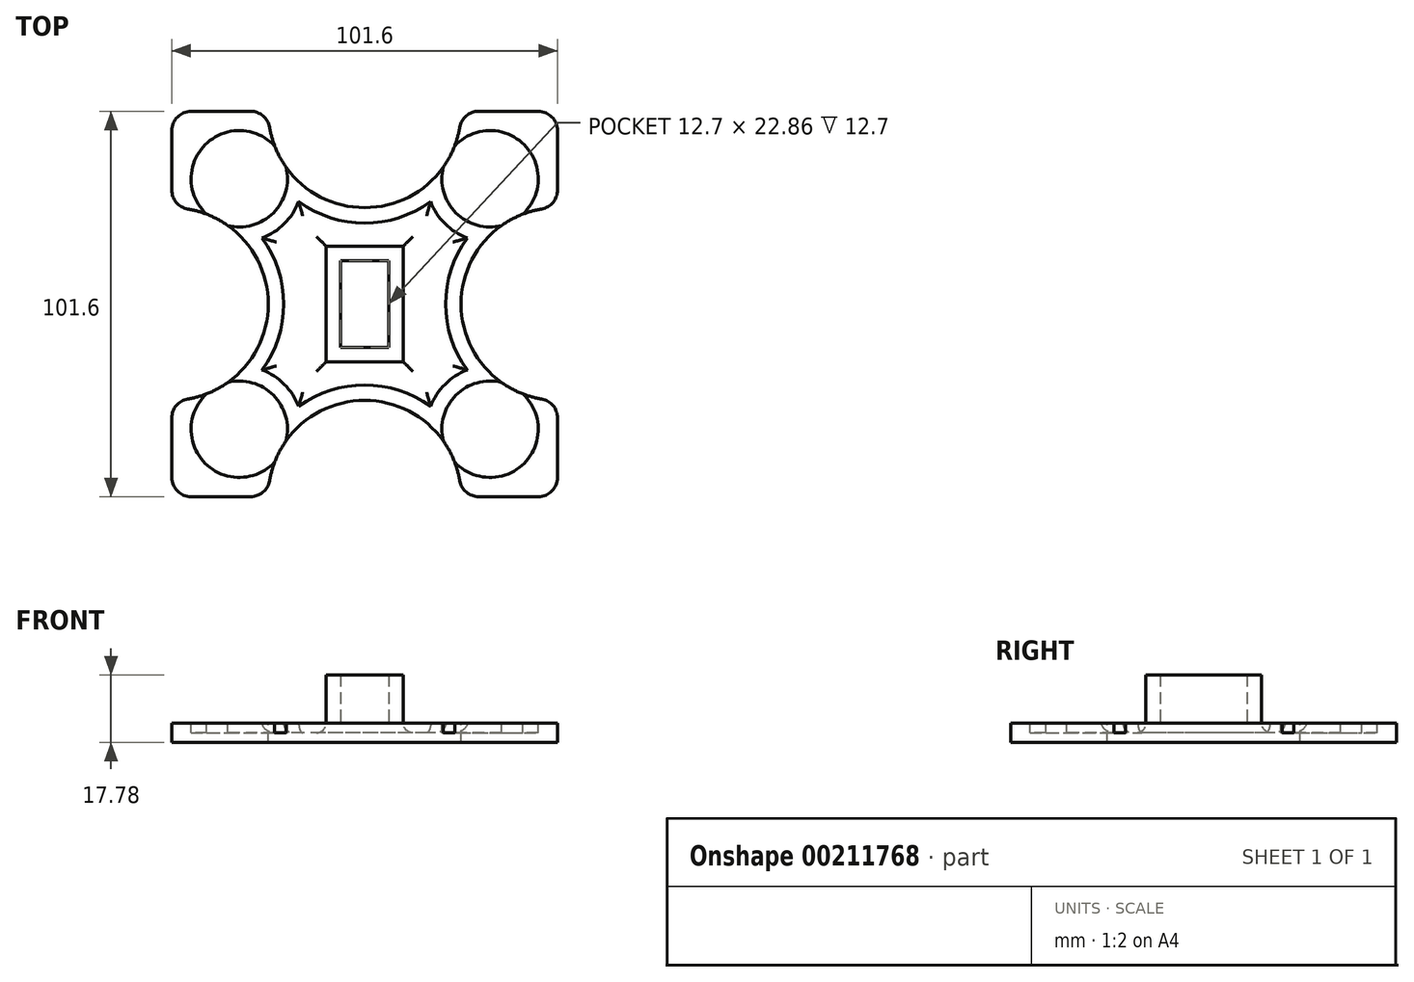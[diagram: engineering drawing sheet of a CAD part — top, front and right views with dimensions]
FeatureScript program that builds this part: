
annotation { "Feature Type Name" : "Feature", "Feature Type Description" : "" }
export const myFeature = defineFeature(function(context is Context, id is Id, definition is map)
    precondition{}
    {
        {
            var Q0;
            Q0=qCreatedBy(makeId("Top.planeOp"),FACE);
            var sketch = newSketch(context, id + "F0", { "sketchPlane" : qUnion([Q0])});
            skLineSegment(sketch, "E0.bottom", {"start": v(50.8, 50.8) * mm, "end": v(-50.8, 50.8) * mm});
            skLineSegment(sketch, "E0.top", {"start": v(50.8, -50.8) * mm, "end": v(-50.8, -50.8) * mm});
            skLineSegment(sketch, "E0.left", {"start": v(50.8, 50.8) * mm, "end": v(50.8, -50.8) * mm});
            skLineSegment(sketch, "E0.right", {"start": v(-50.8, 50.8) * mm, "end": v(-50.8, -50.8) * mm});
            skPoint(sketch, "E0.middle", {"position": v(0, 0) * mm});
            skSolve(sketch);
        }
        {
            var Q0;
            Q0 = qSketchRegion(id + "F0", true);
            var Q1;
            Q1=makeQuery(id+"F0.imprint","IMPRINT",FACE,{"disambiguationData":[TD([[makeQuery(id+"F0.imprint","IMPRINT",EDGE,{"derivedFrom":sQuery(id+"F0.wireOp",EDGE,"E0.bottom")}),1.0]])]});
            extrude(context, id + "F1", {"entities" : qUnion([Q0, Q1]), "depth" : 5.08 * mm});
        }
        {
            var Q0;
            Q0=makeQuery(id+"F1.opExtrude","CAP_FACE",FACE,{"disambiguationData":[OSD([sQuery(id+"F0.wireOp",EDGE,"E0.bottom"),sQuery(id+"F0.wireOp",EDGE,"E0.top"),sQuery(id+"F0.wireOp",EDGE,"E0.left"),sQuery(id+"F0.wireOp",EDGE,"E0.right")])],"isStart":false});
            var sketch = newSketch(context, id + "F2", { "sketchPlane" : qUnion([Q0])});
            skCircle(sketch, "E1", {"center": v(-33.02, 33.02) * mm, "radius": 12.7 * mm});
            skLineSegment(sketch, "E2", {"start": v(0, 54.58) * mm, "end": v(0, -59.94) * mm, "construction": true});
            skLineSegment(sketch, "E3", {"start": v(0, -59.94) * mm, "end": v(60.03, 0) * mm, "construction": true});
            skLineSegment(sketch, "E4", {"start": v(60.03, 0) * mm, "end": v(-63.32, 0) * mm, "construction": true});
            skPoint(sketch, "E4.endSnap0", {"position": v(-50.8, 0) * mm});
            skCircle(sketch, "E5.MirrorC", {"center": v(33.02, 33.02) * mm, "radius": 12.7 * mm});
            skCircle(sketch, "E6.MirrorC", {"center": v(33.02, -33.02) * mm, "radius": 12.7 * mm});
            skCircle(sketch, "E7.MirrorC", {"center": v(-33.02, -33.02) * mm, "radius": 12.7 * mm});
            skSolve(sketch);
        }
        {
            var Q0;
            Q0 = qSketchRegion(id + "F2", true);
            extrude(context, id + "F3", {"entities" : qUnion([Q0]), "operationType" : NewBodyOperationType.REMOVE, "oppositeDirection" : true, "depth" : 2.54 * mm});
        }
        {
            var Q0;
            Q0=makeQuery(id+"F1.opExtrude","CAP_FACE",FACE,{"disambiguationData":[OSD([sQuery(id+"F0.wireOp",EDGE,"E0.bottom"),sQuery(id+"F0.wireOp",EDGE,"E0.top"),sQuery(id+"F0.wireOp",EDGE,"E0.left"),sQuery(id+"F0.wireOp",EDGE,"E0.right")])],"isStart":false});
            var sketch = newSketch(context, id + "F4", { "sketchPlane" : qUnion([Q0])});
            skLineSegment(sketch, "E8.bottom", {"start": v(6.35, 11.43) * mm, "end": v(-6.35, 11.43) * mm});
            skLineSegment(sketch, "E8.top", {"start": v(6.35, -11.43) * mm, "end": v(-6.35, -11.43) * mm});
            skLineSegment(sketch, "E8.left", {"start": v(6.35, 11.43) * mm, "end": v(6.35, -11.43) * mm});
            skLineSegment(sketch, "E8.right", {"start": v(-6.35, 11.43) * mm, "end": v(-6.35, -11.43) * mm});
            skPoint(sketch, "E8.middle", {"position": v(0, 0) * mm});
            skLineSegment(sketch, "E9.0", {"start": v(10.16, 15.24) * mm, "end": v(-10.16, 15.24) * mm});
            skLineSegment(sketch, "E9.1", {"start": v(10.16, 15.24) * mm, "end": v(10.16, -15.24) * mm});
            skLineSegment(sketch, "E9.2", {"start": v(10.16, -15.24) * mm, "end": v(-10.16, -15.24) * mm});
            skLineSegment(sketch, "E9.3", {"start": v(-10.16, 15.24) * mm, "end": v(-10.16, -15.24) * mm});
            skSolve(sketch);
        }
        {
            var Q0;
            Q0 = qSketchRegion(id + "F4", true);
            extrude(context, id + "F5", {"entities" : qUnion([Q0]), "operationType" : NewBodyOperationType.ADD, "depth" : 12.7 * mm});
        }
        {
            var Q0;
            {var subQ0=sQuery(id+"F0.wireOp",EDGE,"E0.top");var subQ1=sQuery(id+"F0.wireOp",EDGE,"E0.bottom");var subQ2=sQuery(id+"F0.wireOp",EDGE,"E0.left");var subQ3=sQuery(id+"F0.wireOp",EDGE,"E0.right");Q0=makeQuery(id+"F5.boolean.opBoolean","SPLIT",FACE,{"disambiguationData":[TD([makeQuery(id+"F1.opExtrude","SWEPT_FACE",FACE,{"disambiguationData":[OSD([subQ1])]})])],"derivedFrom":makeQuery(id+"F1.opExtrude","CAP_FACE",FACE,{"disambiguationData":[OSD([subQ1,subQ0,subQ2,subQ3])],"isStart":false})});}
            var sketch = newSketch(context, id + "F6", { "sketchPlane" : qUnion([Q0])});
            skCircle(sketch, "E10", {"center": v(-50.8, 0) * mm, "radius": 25.4 * mm});
            skCircle(sketch, "E11.MirrorC", {"center": v(50.8, 0) * mm, "radius": 25.4 * mm});
            skCircle(sketch, "E12", {"center": v(0, 50.8) * mm, "radius": 25.4 * mm});
            skCircle(sketch, "E13", {"center": v(0, -50.8) * mm, "radius": 25.4 * mm});
            skSolve(sketch);
        }
        {
            var Q0;
            Q0 = qSketchRegion(id + "F6", true);
            extrude(context, id + "F7", {"entities" : qUnion([Q0]), "operationType" : NewBodyOperationType.REMOVE, "oppositeDirection" : true, "depth" : 25.4 * mm});
        }
        {
            var Q0;
            Q0=makeQuery(id+"F7.boolean.opBoolean","INTERSECT",EDGE,{"disambiguationData":[OD(1.0)],"derivedFrom":[makeQuery(id+"F1.opExtrude","SWEPT_FACE",FACE,{"disambiguationData":[OSD([sQuery(id+"F0.wireOp",EDGE,"E0.right")])]}),makeQuery(id+"F7.opExtrude","SWEPT_FACE",FACE,{"disambiguationData":[OSD([sQuery(id+"F6.wireOp",EDGE,"E10")])]})]});
            var Q1;
            Q1=makeQuery(id+"F1.opExtrude","SWEPT_EDGE",EDGE,{"disambiguationData":[OSD([sQuery(id+"F0.wireOp",EDGE,"E0.top"),sQuery(id+"F0.wireOp",EDGE,"E0.right")])]});
            var Q2;
            Q2=makeQuery(id+"F7.boolean.opBoolean","INTERSECT",EDGE,{"disambiguationData":[OD(1.0)],"derivedFrom":[makeQuery(id+"F1.opExtrude","SWEPT_FACE",FACE,{"disambiguationData":[OSD([sQuery(id+"F0.wireOp",EDGE,"E0.top")])]}),makeQuery(id+"F7.opExtrude","SWEPT_FACE",FACE,{"disambiguationData":[OSD([sQuery(id+"F6.wireOp",EDGE,"E13")])]})]});
            var Q3;
            Q3=makeQuery(id+"F7.boolean.opBoolean","INTERSECT",EDGE,{"disambiguationData":[OD(0.0)],"derivedFrom":[makeQuery(id+"F1.opExtrude","SWEPT_FACE",FACE,{"disambiguationData":[OSD([sQuery(id+"F0.wireOp",EDGE,"E0.top")])]}),makeQuery(id+"F7.opExtrude","SWEPT_FACE",FACE,{"disambiguationData":[OSD([sQuery(id+"F6.wireOp",EDGE,"E13")])]})]});
            var Q4;
            Q4=makeQuery(id+"F1.opExtrude","SWEPT_EDGE",EDGE,{"disambiguationData":[OSD([sQuery(id+"F0.wireOp",EDGE,"E0.top"),sQuery(id+"F0.wireOp",EDGE,"E0.left")])]});
            var Q5;
            Q5=makeQuery(id+"F7.boolean.opBoolean","INTERSECT",EDGE,{"disambiguationData":[OD(1.0)],"derivedFrom":[makeQuery(id+"F1.opExtrude","SWEPT_FACE",FACE,{"disambiguationData":[OSD([sQuery(id+"F0.wireOp",EDGE,"E0.left")])]}),makeQuery(id+"F7.opExtrude","SWEPT_FACE",FACE,{"disambiguationData":[OSD([sQuery(id+"F6.wireOp",EDGE,"E11.MirrorC")])]})]});
            var Q6;
            Q6=makeQuery(id+"F7.boolean.opBoolean","INTERSECT",EDGE,{"disambiguationData":[OD(0.0)],"derivedFrom":[makeQuery(id+"F1.opExtrude","SWEPT_FACE",FACE,{"disambiguationData":[OSD([sQuery(id+"F0.wireOp",EDGE,"E0.left")])]}),makeQuery(id+"F7.opExtrude","SWEPT_FACE",FACE,{"disambiguationData":[OSD([sQuery(id+"F6.wireOp",EDGE,"E11.MirrorC")])]})]});
            var Q7;
            Q7=makeQuery(id+"F1.opExtrude","SWEPT_EDGE",EDGE,{"disambiguationData":[OSD([sQuery(id+"F0.wireOp",EDGE,"E0.bottom"),sQuery(id+"F0.wireOp",EDGE,"E0.left")])]});
            var Q8;
            Q8=makeQuery(id+"F7.boolean.opBoolean","INTERSECT",EDGE,{"disambiguationData":[OD(0.0)],"derivedFrom":[makeQuery(id+"F1.opExtrude","SWEPT_FACE",FACE,{"disambiguationData":[OSD([sQuery(id+"F0.wireOp",EDGE,"E0.bottom")])]}),makeQuery(id+"F7.opExtrude","SWEPT_FACE",FACE,{"disambiguationData":[OSD([sQuery(id+"F6.wireOp",EDGE,"E12")])]})]});
            var Q9;
            Q9=makeQuery(id+"F7.boolean.opBoolean","INTERSECT",EDGE,{"disambiguationData":[OD(1.0)],"derivedFrom":[makeQuery(id+"F1.opExtrude","SWEPT_FACE",FACE,{"disambiguationData":[OSD([sQuery(id+"F0.wireOp",EDGE,"E0.bottom")])]}),makeQuery(id+"F7.opExtrude","SWEPT_FACE",FACE,{"disambiguationData":[OSD([sQuery(id+"F6.wireOp",EDGE,"E12")])]})]});
            var Q10;
            Q10=makeQuery(id+"F1.opExtrude","SWEPT_EDGE",EDGE,{"disambiguationData":[OSD([sQuery(id+"F0.wireOp",EDGE,"E0.bottom"),sQuery(id+"F0.wireOp",EDGE,"E0.right")])]});
            var Q11;
            Q11=makeQuery(id+"F7.boolean.opBoolean","INTERSECT",EDGE,{"disambiguationData":[OD(0.0)],"derivedFrom":[makeQuery(id+"F1.opExtrude","SWEPT_FACE",FACE,{"disambiguationData":[OSD([sQuery(id+"F0.wireOp",EDGE,"E0.right")])]}),makeQuery(id+"F7.opExtrude","SWEPT_FACE",FACE,{"disambiguationData":[OSD([sQuery(id+"F6.wireOp",EDGE,"E10")])]})]});
            fillet(context, id + "F8", {"entities" : qUnion([Q0, Q1, Q2, Q3, Q4, Q5, Q6, Q7, Q8, Q9, Q10, Q11]), "radius" : 5.08 * mm, "tangentPropagation" : true, "allowEdgeOverflow" : false});
        }
        {
            var Q0;
            {var subQ0=makeQuery(id+"F5.opExtrude","SWEPT_FACE",FACE,{"disambiguationData":[OSD([sQuery(id+"F4.wireOp",EDGE,"E9.3")])]});var subQ1=makeQuery(id+"F5.opExtrude","SWEPT_FACE",FACE,{"disambiguationData":[OSD([sQuery(id+"F4.wireOp",EDGE,"E9.0")])]});var subQ2=makeQuery(id+"F3.boolean.opBoolean","COPY",FACE,{"derivedFrom":makeQuery(id+"F3.opExtrude","SWEPT_FACE",FACE,{"disambiguationData":[OSD([sQuery(id+"F2.wireOp",EDGE,"E1")])]})});var subQ3=makeQuery(id+"F5.opExtrude","SWEPT_FACE",FACE,{"disambiguationData":[OSD([sQuery(id+"F4.wireOp",EDGE,"E9.1")])]});var subQ4=makeQuery(id+"F3.boolean.opBoolean","COPY",FACE,{"derivedFrom":makeQuery(id+"F3.opExtrude","SWEPT_FACE",FACE,{"disambiguationData":[OSD([sQuery(id+"F2.wireOp",EDGE,"E5.MirrorC")])]})});var subQ5=makeQuery(id+"F5.opExtrude","SWEPT_FACE",FACE,{"disambiguationData":[OSD([sQuery(id+"F4.wireOp",EDGE,"E9.2")])]});var subQ6=makeQuery(id+"F3.boolean.opBoolean","COPY",FACE,{"derivedFrom":makeQuery(id+"F3.opExtrude","SWEPT_FACE",FACE,{"disambiguationData":[OSD([sQuery(id+"F2.wireOp",EDGE,"E6.MirrorC")])]})});var subQ7=makeQuery(id+"F3.boolean.opBoolean","COPY",FACE,{"derivedFrom":makeQuery(id+"F3.opExtrude","SWEPT_FACE",FACE,{"disambiguationData":[OSD([sQuery(id+"F2.wireOp",EDGE,"E7.MirrorC")])]})});var subQ8=sQuery(id+"F0.wireOp",EDGE,"E0.top");var subQ9=sQuery(id+"F0.wireOp",EDGE,"E0.bottom");var subQ10=sQuery(id+"F0.wireOp",EDGE,"E0.left");var subQ11=sQuery(id+"F0.wireOp",EDGE,"E0.right");Q0=makeQuery(id+"F7.boolean.opBoolean","SPLIT",FACE,{"disambiguationData":[TD([subQ2,subQ4,subQ6,subQ7,subQ1,subQ3,subQ5,subQ0,makeQuery(id+"F7.opExtrude","SWEPT_FACE",FACE,{"disambiguationData":[OSD([sQuery(id+"F6.wireOp",EDGE,"E10")])]}),makeQuery(id+"F7.opExtrude","SWEPT_FACE",FACE,{"disambiguationData":[OSD([sQuery(id+"F6.wireOp",EDGE,"E11.MirrorC")])]}),makeQuery(id+"F7.opExtrude","SWEPT_FACE",FACE,{"disambiguationData":[OSD([sQuery(id+"F6.wireOp",EDGE,"E12")])]}),makeQuery(id+"F7.opExtrude","SWEPT_FACE",FACE,{"disambiguationData":[OSD([sQuery(id+"F6.wireOp",EDGE,"E13")])]})])],"derivedFrom":makeQuery(id+"F5.boolean.opBoolean","SPLIT",FACE,{"disambiguationData":[TD([makeQuery(id+"F1.opExtrude","SWEPT_FACE",FACE,{"disambiguationData":[OSD([subQ9])]})])],"derivedFrom":makeQuery(id+"F1.opExtrude","CAP_FACE",FACE,{"disambiguationData":[OSD([subQ9,subQ8,subQ10,subQ11])],"isStart":false})})});}
            var sketch = newSketch(context, id + "F9", { "sketchPlane" : qUnion([Q0])});
            skArc(sketch, "E14.0", {"start": v(27, 17.37) * mm, "mid": v(21.17, 21.17) * mm, "end": v(17.37, 27) * mm});
            skArc(sketch, "E14.1", {"start": v(27, -17.37) * mm, "mid": v(21.34, 0) * mm, "end": v(27, 17.37) * mm});
            skArc(sketch, "E14.2", {"start": v(17.37, 27) * mm, "mid": v(0, 21.34) * mm, "end": v(-17.37, 27) * mm});
            skArc(sketch, "E14.3", {"start": v(17.37, -27) * mm, "mid": v(21.17, -21.17) * mm, "end": v(27, -17.37) * mm});
            skArc(sketch, "E14.4", {"start": v(-17.37, 27) * mm, "mid": v(-21.17, 21.17) * mm, "end": v(-27, 17.37) * mm});
            skArc(sketch, "E14.5", {"start": v(-27, 17.37) * mm, "mid": v(-21.34, 0) * mm, "end": v(-27, -17.37) * mm});
            skArc(sketch, "E14.6", {"start": v(-27, -17.37) * mm, "mid": v(-21.17, -21.17) * mm, "end": v(-17.37, -27) * mm});
            skArc(sketch, "E14.7", {"start": v(-17.37, -27) * mm, "mid": v(0, -21.34) * mm, "end": v(17.37, -27) * mm});
            skLineSegment(sketch, "E15.0", {"start": v(-10.16, 15.24) * mm, "end": v(-10.16, -15.24) * mm});
            skLineSegment(sketch, "E15.1", {"start": v(10.16, 15.24) * mm, "end": v(-10.16, 15.24) * mm});
            skLineSegment(sketch, "E15.2", {"start": v(10.16, 15.24) * mm, "end": v(10.16, -15.24) * mm});
            skLineSegment(sketch, "E15.3", {"start": v(10.16, -15.24) * mm, "end": v(-10.16, -15.24) * mm});
            skSolve(sketch);
        }
        {
            var Q0;
            Q0 = qSketchRegion(id + "F9", true);
            extrude(context, id + "F10", {"entities" : qUnion([Q0]), "operationType" : NewBodyOperationType.REMOVE, "oppositeDirection" : true, "depth" : 2.54 * mm});
        }
        {
            var Q0;
            Q0=makeQuery(id+"F10.boolean.opBoolean","COPY",FACE,{"derivedFrom":makeQuery(id+"F10.opExtrude","CAP_FACE",FACE,{"disambiguationData":[OSD([sQuery(id+"F9.wireOp",EDGE,"E14.0"),sQuery(id+"F9.wireOp",EDGE,"E14.1"),sQuery(id+"F9.wireOp",EDGE,"E14.2"),sQuery(id+"F9.wireOp",EDGE,"E14.3"),sQuery(id+"F9.wireOp",EDGE,"E14.4"),sQuery(id+"F9.wireOp",EDGE,"E14.5"),sQuery(id+"F9.wireOp",EDGE,"E14.6"),sQuery(id+"F9.wireOp",EDGE,"E14.7"),sQuery(id+"F9.wireOp",EDGE,"E15.0"),sQuery(id+"F9.wireOp",EDGE,"E15.1"),sQuery(id+"F9.wireOp",EDGE,"E15.2"),sQuery(id+"F9.wireOp",EDGE,"E15.3")])],"isStart":false})});
            fillet(context, id + "F11", {"entities" : qUnion([Q0]), "radius" : 2.54 * mm, "tangentPropagation" : true, "allowEdgeOverflow" : false});
        }
    });
